# Revit family: Mark Ecofan W
name_source: partatom
category: Mechanical Equipment
revit_build: Autodesk Revit 2016 (Build: 20150714_1515(x64)
units: mm (PartAtom-declared; Revit-internal decimal feet)

## family parameters
Always vertical = Yes
Cut with Voids When Loaded = No
OmniClass Number = 23.75.00.00
OmniClass Title = Climate Control (HVAC)
Part Type = Normal
Room Calculation Point = No
Round Connector Dimension = Use Diameter
Shared = No
Work Plane-Based = No

## types (1)
- Ecofan W type W82
    Manufacturer = Mark
    Model = ECOFAN W
    Type Comments = Type W82
    URL = http://www.mark.nl
    aantal_polen = 1
    b1 = 720 mm  [stored 2.3622 ft]
    b2 = 600 mm
    breedte = 720 mm  [stored 2.3622 ft]
    debiet = 800.0 m³/h
    elektrisch_vermogen = 360 W
    gewicht = 23 KG
    h1 = 265 mm  [stored 0.869423 ft]
    h2 = 165 mm
    hoogte = 265 mm  [stored 0.869423 ft]
    lengte = 720 mm  [stored 2.3622 ft]
    nominale stroom = 2 A
    schijnbaar_vermogen = 391 VA
    voltage = 230 V

note: [stored X ft] marks values corroborated as IEEE doubles in the binary element streams (Revit-internal decimal feet)

## geometry (parser evidence)
native form markers: Sweep x3
no freeform markers — native parametric forms only
